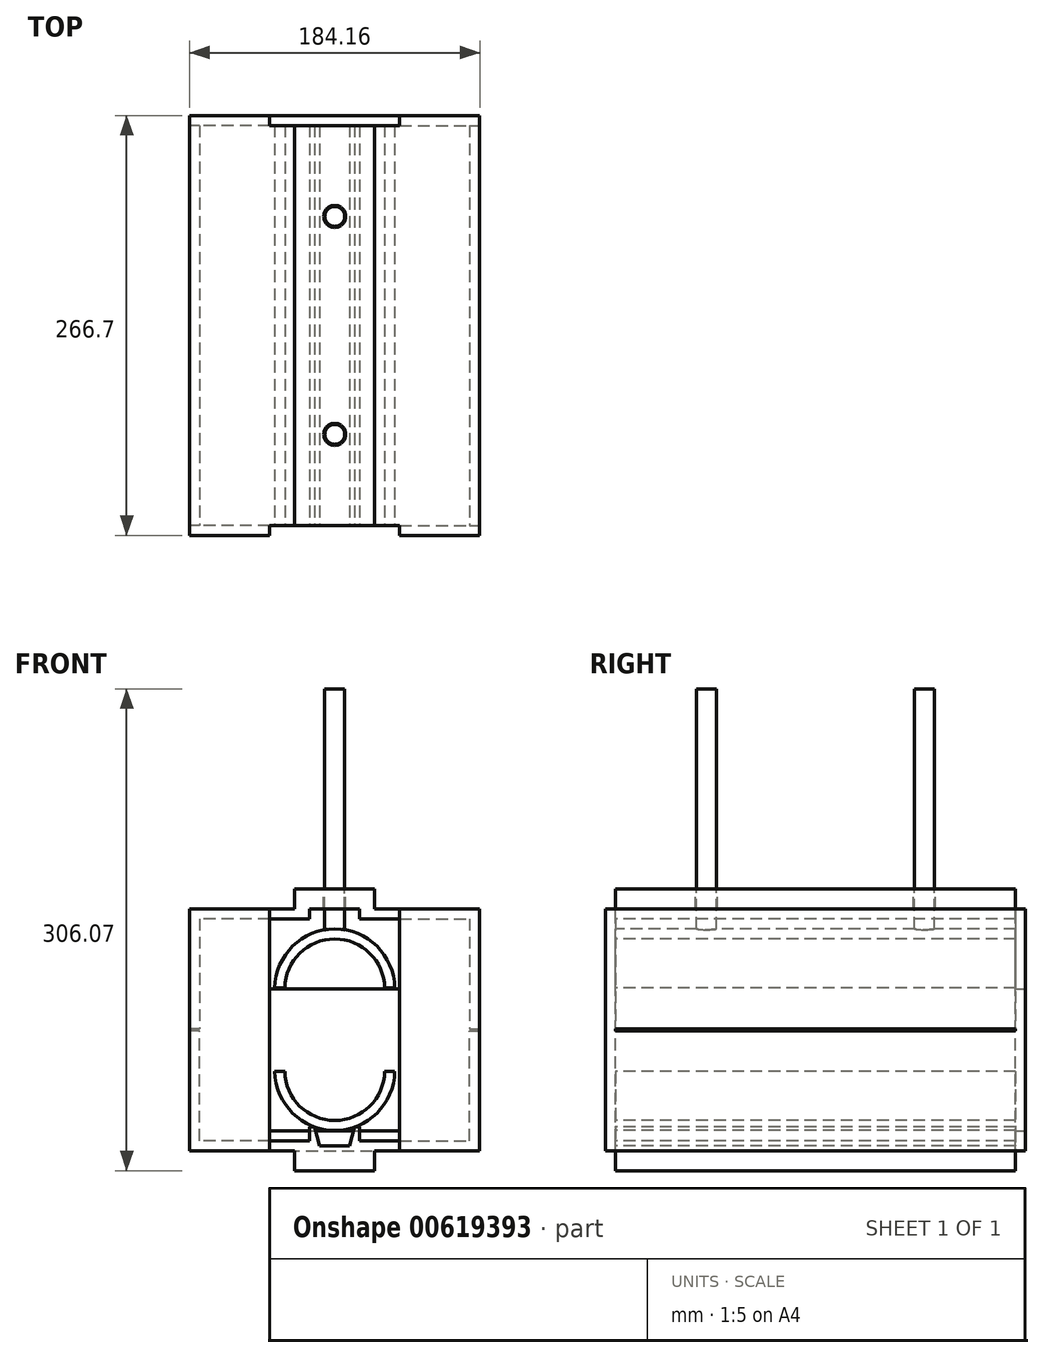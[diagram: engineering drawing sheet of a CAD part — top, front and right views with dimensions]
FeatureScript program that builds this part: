
annotation { "Feature Type Name" : "Feature", "Feature Type Description" : "" }
export const myFeature = defineFeature(function(context is Context, id is Id, definition is map)
    precondition{}
    {
        {
            var Q0;
            Q0=qCreatedBy(makeId("Top.planeOp"),FACE);
            cPlane(context, id + "F0", {"entities" : qUnion([Q0]), "cplaneType" : CPlaneType.OFFSET, "offset" : 0.64 * mm, "width" : 152.4 * mm, "height" : 152.4 * mm});
        }
        {
            var Q0;
            Q0=qCreatedBy(makeId("Front.planeOp"),FACE);
            var sketch = newSketch(context, id + "F1", { "sketchPlane" : qUnion([Q0])});
            skCircle(sketch, "E0", {"center": v(0, 0) * mm, "radius": 31.75 * mm, "construction": true});
            skLineSegment(sketch, "E1", {"start": v(0, 76.2) * mm, "end": v(0, -76.2) * mm, "construction": true});
            skLineSegment(sketch, "E2", {"start": v(-92.08, 0) * mm, "end": v(-92.08, -76.2) * mm});
            skLineSegment(sketch, "E3", {"start": v(-92.08, -76.2) * mm, "end": v(-15.87, -76.2) * mm});
            skLineSegment(sketch, "E4", {"start": v(-15.87, -76.2) * mm, "end": v(-15.87, -69.85) * mm});
            skLineSegment(sketch, "E5", {"start": v(-15.87, -69.85) * mm, "end": v(-85.73, -69.85) * mm});
            skLineSegment(sketch, "E6", {"start": v(-85.73, -69.85) * mm, "end": v(-85.73, 0) * mm});
            skLineSegment(sketch, "E7", {"start": v(-85.73, 0) * mm, "end": v(-92.08, 0) * mm});
            skLineSegment(sketch, "E8", {"start": v(-15.87, -76.2) * mm, "end": v(-15.87, -61.18) * mm});
            skLineSegment(sketch, "E9", {"start": v(-15.87, -61.18) * mm, "end": v(-12.7, -61.18) * mm});
            skLineSegment(sketch, "E10", {"start": v(-12.7, -61.18) * mm, "end": v(-9.52, -73.03) * mm});
            skLineSegment(sketch, "E11", {"start": v(-9.52, -73.03) * mm, "end": v(9.53, -73.03) * mm});
            skLineSegment(sketch, "E12", {"start": v(9.53, -73.03) * mm, "end": v(12.7, -61.18) * mm});
            skLineSegment(sketch, "E13", {"start": v(12.7, -61.18) * mm, "end": v(15.88, -61.18) * mm});
            skLineSegment(sketch, "E14", {"start": v(15.88, -61.18) * mm, "end": v(15.88, -76.2) * mm});
            skLineSegment(sketch, "E15", {"start": v(15.88, -76.2) * mm, "end": v(-15.87, -76.2) * mm});
            skLineSegment(sketch, "E16.MirrorCS", {"start": v(92.08, -76.2) * mm, "end": v(15.87, -76.2) * mm});
            skLineSegment(sketch, "E17.MirrorCS", {"start": v(15.87, -69.85) * mm, "end": v(85.73, -69.85) * mm});
            skLineSegment(sketch, "E18.MirrorCS", {"start": v(92.08, 0) * mm, "end": v(92.08, -76.2) * mm});
            skLineSegment(sketch, "E19.MirrorCS", {"start": v(85.73, -69.85) * mm, "end": v(85.73, 0) * mm});
            skLineSegment(sketch, "E20.MirrorCS", {"start": v(85.73, 0) * mm, "end": v(92.08, 0) * mm});
            skLineSegment(sketch, "E21.bottom", {"start": v(-25.4, -76.2) * mm, "end": v(25.4, -76.2) * mm});
            skLineSegment(sketch, "E21.top", {"start": v(-25.4, -88.9) * mm, "end": v(25.4, -88.9) * mm});
            skLineSegment(sketch, "E21.left", {"start": v(-25.4, -76.2) * mm, "end": v(-25.4, -88.9) * mm});
            skLineSegment(sketch, "E21.right", {"start": v(25.4, -76.2) * mm, "end": v(25.4, -88.9) * mm});
            skLineSegment(sketch, "E22", {"start": v(0, -76.2) * mm, "end": v(0, -88.9) * mm, "construction": true});
            skLineSegment(sketch, "E23.MirrorCS", {"start": v(-85.73, 1.27) * mm, "end": v(-92.08, 1.27) * mm});
            skLineSegment(sketch, "E24.MirrorCS", {"start": v(-92.08, 1.27) * mm, "end": v(-92.08, 77.47) * mm});
            skLineSegment(sketch, "E25.MirrorCS", {"start": v(-85.73, 71.12) * mm, "end": v(-85.73, 1.27) * mm});
            skLineSegment(sketch, "E26.MirrorCS", {"start": v(-15.87, 71.12) * mm, "end": v(-85.73, 71.12) * mm});
            skLineSegment(sketch, "E27.MirrorCS", {"start": v(-92.08, 77.47) * mm, "end": v(-15.87, 77.47) * mm});
            skLineSegment(sketch, "E28.MirrorCS", {"start": v(-25.4, 77.47) * mm, "end": v(-25.4, 90.17) * mm});
            skLineSegment(sketch, "E29.MirrorCS", {"start": v(-25.4, 90.17) * mm, "end": v(25.4, 90.17) * mm});
            skLineSegment(sketch, "E30.MirrorCS", {"start": v(25.4, 77.47) * mm, "end": v(25.4, 90.17) * mm});
            skLineSegment(sketch, "E31.MirrorCS", {"start": v(92.08, 77.47) * mm, "end": v(15.87, 77.47) * mm});
            skLineSegment(sketch, "E32.MirrorCS", {"start": v(15.87, 71.12) * mm, "end": v(85.73, 71.12) * mm});
            skLineSegment(sketch, "E33.MirrorCS", {"start": v(85.73, 71.12) * mm, "end": v(85.73, 1.27) * mm});
            skLineSegment(sketch, "E34.MirrorCS", {"start": v(92.08, 1.27) * mm, "end": v(92.08, 77.47) * mm});
            skLineSegment(sketch, "E35.MirrorCS", {"start": v(85.73, 1.27) * mm, "end": v(92.08, 1.27) * mm});
            skLineSegment(sketch, "E36", {"start": v(-25.4, 77.47) * mm, "end": v(25.4, 77.47) * mm});
            skLineSegment(sketch, "E37", {"start": v(-15.87, 77.47) * mm, "end": v(-15.87, 71.12) * mm});
            skLineSegment(sketch, "E38", {"start": v(15.87, 77.47) * mm, "end": v(15.87, 71.12) * mm});
            skSolve(sketch);
        }
        {
            var Q0;
            Q0 = qSketchRegion(id + "F1", true);
            extrude(context, id + "F2", {"entities" : qUnion([Q0]), "oppositeDirection" : true, "depth" : 254 * mm, "offsetDistance" : 25.4 * mm});
        }
        {
            var Q0;
            Q0=qCreatedBy(makeId("Front.planeOp"),FACE);
            var sketch = newSketch(context, id + "F3", { "sketchPlane" : qUnion([Q0])});
            skArc(sketch, "E39", {"start": v(-31.74, -25.89) * mm, "mid": v(0, -57) * mm, "end": v(31.74, -25.89) * mm});
            skArc(sketch, "E40", {"start": v(-38.1, -25.89) * mm, "mid": v(0, -63.35) * mm, "end": v(38.1, -25.89) * mm});
            skLineSegment(sketch, "E41", {"start": v(38.1, -25.25) * mm, "end": v(-38.1, -25.25) * mm, "construction": true});
            skLineSegment(sketch, "E42", {"start": v(-38.1, -24.62) * mm, "end": v(-31.74, -24.62) * mm, "construction": true});
            skLineSegment(sketch, "E43.MirrorCS", {"start": v(-38.1, -25.89) * mm, "end": v(-31.74, -25.89) * mm});
            skArc(sketch, "E44.trimOffspring", {"start": v(38.1, -24.62) * mm, "mid": v(0, 12.85) * mm, "end": v(-38.1, -24.62) * mm, "construction": true});
            skLineSegment(sketch, "E45.trimOffspring", {"start": v(31.74, -25.89) * mm, "end": v(38.1, -25.89) * mm});
            skLineSegment(sketch, "E46.trimOffspring", {"start": v(31.74, -24.62) * mm, "end": v(38.1, -24.62) * mm, "construction": true});
            skArc(sketch, "E47.trimOffspring", {"start": v(31.74, -24.62) * mm, "mid": v(0, 6.5) * mm, "end": v(-31.74, -24.62) * mm, "construction": true});
            skLineSegment(sketch, "E48.MirrorCS", {"start": v(-38.1, 27.16) * mm, "end": v(-31.74, 27.16) * mm});
            skArc(sketch, "E49.MirrorCS", {"start": v(-38.1, 27.16) * mm, "mid": v(0, 64.62) * mm, "end": v(38.1, 27.16) * mm});
            skArc(sketch, "E50.MirrorCS", {"start": v(-31.74, 27.16) * mm, "mid": v(0, 58.27) * mm, "end": v(31.74, 27.16) * mm});
            skLineSegment(sketch, "E51.MirrorCS", {"start": v(31.74, 27.16) * mm, "end": v(38.1, 27.16) * mm});
            skSolve(sketch);
        }
        {
            var Q0;
            Q0 = qSketchRegion(id + "F3", true);
            extrude(context, id + "F4", {"entities" : qUnion([Q0]), "operationType" : NewBodyOperationType.ADD, "oppositeDirection" : true, "depth" : 254 * mm, "offsetDistance" : 25.4 * mm});
        }
        {
            var Q0;
            Q0=makeQuery(id+"F2.opExtrude","SWEPT_FACE",FACE,{"disambiguationData":[OSD([sQuery(id+"F1.wireOp",EDGE,"E29.MirrorCS")])]});
            var sketch = newSketch(context, id + "F5", { "sketchPlane" : qUnion([Q0])});
            skLineSegment(sketch, "E52", {"start": v(0, 254) * mm, "end": v(0, 0) * mm, "construction": true});
            skLineSegment(sketch, "E53", {"start": v(-25.4, 127) * mm, "end": v(25.4, 127) * mm, "construction": true});
            skCircle(sketch, "E54", {"center": v(0, 196.22) * mm, "radius": 6.99 * mm});
            skCircle(sketch, "E55.MirrorC", {"center": v(0, 57.79) * mm, "radius": 6.99 * mm});
            skSolve(sketch);
        }
        {
            var Q0;
            Q0 = qSketchRegion(id + "F5", true);
            var Q1;
            Q1=makeQuery(id+"F2.opExtrude","SWEPT_FACE",FACE,{"disambiguationData":[OSD([sQuery(id+"F1.wireOp",EDGE,"E36")])]});
            extrude(context, id + "F6", {"entities" : qUnion([Q0]), "operationType" : NewBodyOperationType.REMOVE, "endBound" : BoundingType.UP_TO_SURFACE, "oppositeDirection" : true, "depth" : 25.4 * mm, "endBoundEntityFace" : qUnion([Q1]), "offsetDistance" : 25.4 * mm});
        }
        {
            var Q0;
            Q0=makeQuery(id+"F2.opExtrude","SWEPT_FACE",FACE,{"disambiguationData":[OSD([sQuery(id+"F1.wireOp",EDGE,"E29.MirrorCS")])]});
            cPlane(context, id + "F7", {"entities" : qUnion([Q0]), "cplaneType" : CPlaneType.OFFSET, "offset" : 127 * mm, "width" : 152.4 * mm, "height" : 152.4 * mm});
        }
        {
            var Q0;
            Q0=qCreatedBy(id+"F7.planeOp",FACE);
            var sketch = newSketch(context, id + "F8", { "sketchPlane" : qUnion([Q0])});
            skCircle(sketch, "E56", {"center": v(0, 196.22) * mm, "radius": 6.35 * mm});
            skCircle(sketch, "E57", {"center": v(0, 57.79) * mm, "radius": 6.35 * mm});
            skSolve(sketch);
        }
        {
            var Q0;
            Q0 = qSketchRegion(id + "F8", true);
            var Q1;
            Q1=makeQuery(id+"F4.opExtrude","SWEPT_FACE",FACE,{"disambiguationData":[OSD([sQuery(id+"F3.wireOp",EDGE,"E49.MirrorCS")])]});
            extrude(context, id + "F9", {"entities" : qUnion([Q0]), "operationType" : NewBodyOperationType.ADD, "endBound" : BoundingType.UP_TO_SURFACE, "oppositeDirection" : true, "depth" : 25.4 * mm, "endBoundEntityFace" : qUnion([Q1]), "offsetDistance" : 25.4 * mm});
        }
        {
            var Q0;
            Q0=makeQuery(id+"F2.opExtrude","SWEPT_FACE",FACE,{"disambiguationData":[OSD([sQuery(id+"F1.wireOp",EDGE,"E27.MirrorCS")])]});
            var sketch = newSketch(context, id + "F10", { "sketchPlane" : qUnion([Q0])});
            skLineSegment(sketch, "E58.bottom", {"start": v(-92.07, 0) * mm, "end": v(-41.27, 0) * mm});
            skLineSegment(sketch, "E58.top", {"start": v(-92.07, -6.35) * mm, "end": v(-41.27, -6.35) * mm});
            skLineSegment(sketch, "E58.left", {"start": v(-92.07, 0) * mm, "end": v(-92.07, -6.35) * mm});
            skLineSegment(sketch, "E58.right", {"start": v(-41.27, 0) * mm, "end": v(-41.27, -6.35) * mm});
            skLineSegment(sketch, "E59.MirrorCS", {"start": v(92.08, -6.35) * mm, "end": v(41.28, -6.35) * mm});
            skLineSegment(sketch, "E60.MirrorCS", {"start": v(92.08, 0) * mm, "end": v(41.28, 0) * mm});
            skLineSegment(sketch, "E61.MirrorCS", {"start": v(41.28, 0) * mm, "end": v(41.28, -6.35) * mm});
            skLineSegment(sketch, "E62.MirrorCS", {"start": v(92.08, 0) * mm, "end": v(92.08, -6.35) * mm});
            skLineSegment(sketch, "E63", {"start": v(-92.08, 127) * mm, "end": v(-25.4, 127) * mm, "construction": true});
            skLineSegment(sketch, "E64.MirrorCS", {"start": v(-92.07, 254) * mm, "end": v(-41.27, 254) * mm});
            skLineSegment(sketch, "E65.MirrorCS", {"start": v(-41.27, 254) * mm, "end": v(-41.27, 260.35) * mm});
            skLineSegment(sketch, "E66.MirrorCS", {"start": v(-92.07, 260.35) * mm, "end": v(-41.27, 260.35) * mm});
            skLineSegment(sketch, "E67.MirrorCS", {"start": v(-92.07, 254) * mm, "end": v(-92.07, 260.35) * mm});
            skLineSegment(sketch, "E68.MirrorCS", {"start": v(92.08, 254) * mm, "end": v(41.28, 254) * mm});
            skLineSegment(sketch, "E69.MirrorCS", {"start": v(92.08, 260.35) * mm, "end": v(41.28, 260.35) * mm});
            skLineSegment(sketch, "E70.MirrorCS", {"start": v(92.08, 254) * mm, "end": v(92.08, 260.35) * mm});
            skLineSegment(sketch, "E71.MirrorCS", {"start": v(41.28, 254) * mm, "end": v(41.28, 260.35) * mm});
            skSolve(sketch);
        }
        {
            var Q0;
            Q0 = qSketchRegion(id + "F10", true);
            var Q1;
            Q1=makeQuery(id+"F2.opExtrude","SWEPT_FACE",FACE,{"disambiguationData":[OSD([sQuery(id+"F1.wireOp",EDGE,"E3")])]});
            extrude(context, id + "F11", {"entities" : qUnion([Q0]), "operationType" : NewBodyOperationType.ADD, "endBound" : BoundingType.UP_TO_SURFACE, "oppositeDirection" : true, "depth" : 25.4 * mm, "endBoundEntityFace" : qUnion([Q1]), "offsetDistance" : 25.4 * mm});
        }
        {
            var Q0;
            Q0=makeQuery(id+"F11.opExtrude","SWEPT_FACE",FACE,{"disambiguationData":[OSD([sQuery(id+"F10.wireOp",EDGE,"E71.MirrorCS")])]});
            var sketch = newSketch(context, id + "F12", { "sketchPlane" : qUnion([Q0])});
            skLineSegment(sketch, "E72.bottom", {"start": v(-260.35, -76.2) * mm, "end": v(-254, -76.2) * mm});
            skLineSegment(sketch, "E72.top", {"start": v(-260.35, -63.5) * mm, "end": v(-254, -63.5) * mm});
            skLineSegment(sketch, "E72.left", {"start": v(-260.35, -76.2) * mm, "end": v(-260.35, -63.5) * mm});
            skLineSegment(sketch, "E72.right", {"start": v(-254, -76.2) * mm, "end": v(-254, -63.5) * mm});
            skLineSegment(sketch, "E73.bottom", {"start": v(-260.35, 77.47) * mm, "end": v(-254, 77.47) * mm});
            skLineSegment(sketch, "E73.top", {"start": v(-260.35, 26.67) * mm, "end": v(-254, 26.67) * mm});
            skLineSegment(sketch, "E73.left", {"start": v(-260.35, 77.47) * mm, "end": v(-260.35, 26.67) * mm});
            skLineSegment(sketch, "E73.right", {"start": v(-254, 77.47) * mm, "end": v(-254, 26.67) * mm});
            skSolve(sketch);
        }
        {
            var Q0;
            Q0 = qSketchRegion(id + "F12", true);
            var Q1;
            Q1=makeQuery(id+"F11.opExtrude","SWEPT_FACE",FACE,{"disambiguationData":[OSD([sQuery(id+"F10.wireOp",EDGE,"E65.MirrorCS")])]});
            extrude(context, id + "F13", {"entities" : qUnion([Q0]), "endBound" : BoundingType.UP_TO_SURFACE, "depth" : 25.4 * mm, "endBoundEntityFace" : qUnion([Q1]), "offsetDistance" : 25.4 * mm});
        }
    });
